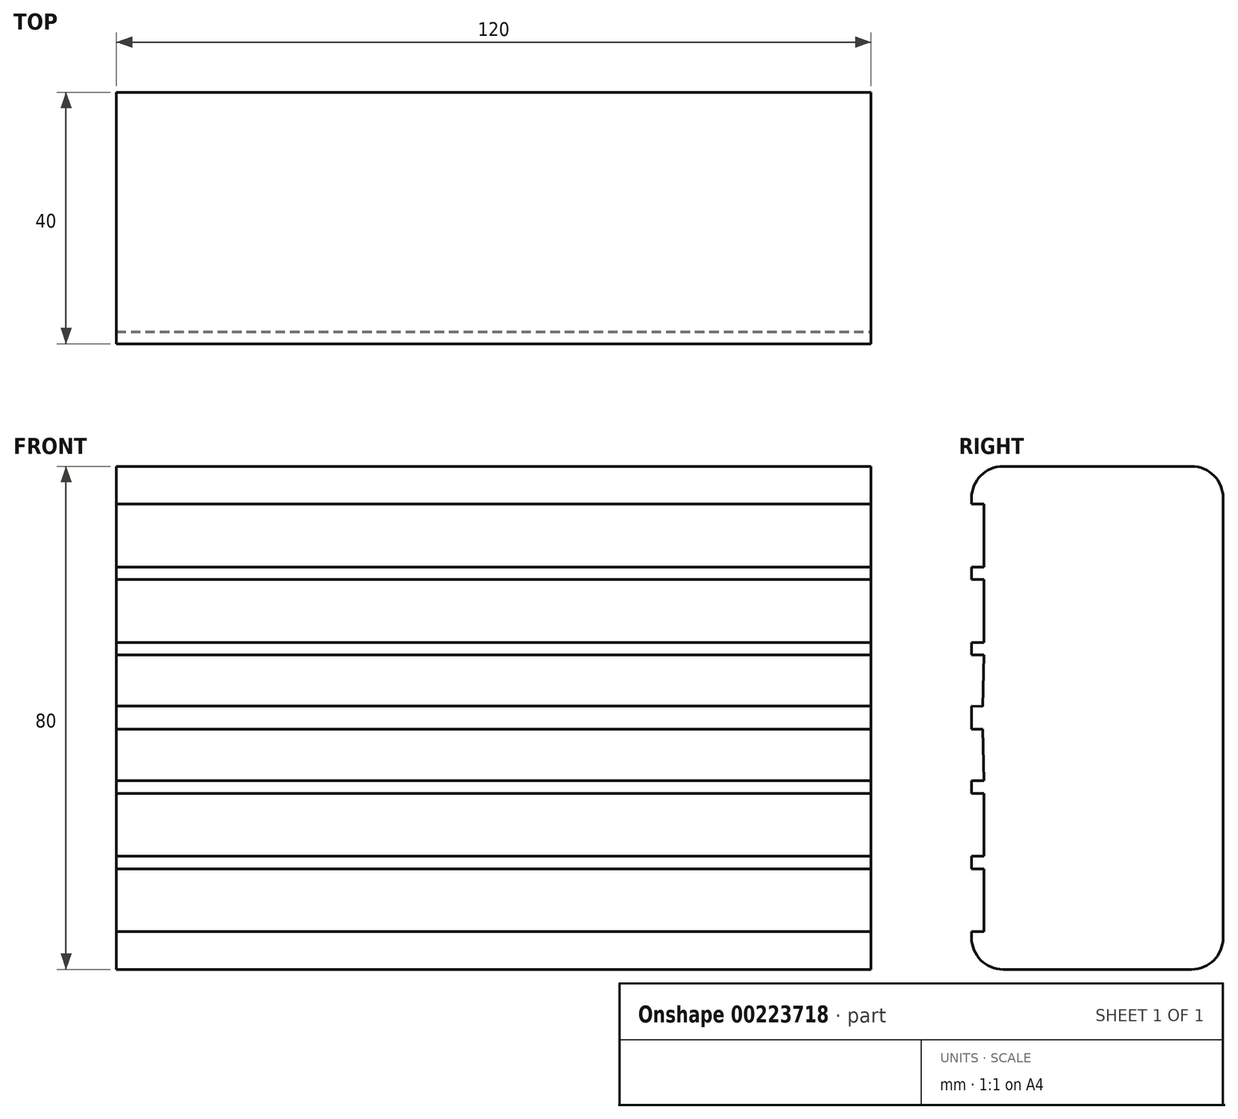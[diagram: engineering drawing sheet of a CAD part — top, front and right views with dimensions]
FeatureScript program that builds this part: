
annotation { "Feature Type Name" : "Feature", "Feature Type Description" : "" }
export const myFeature = defineFeature(function(context is Context, id is Id, definition is map)
    precondition{}
    {
        {
            var Q0;
            Q0=qCreatedBy(makeId("Front.planeOp"),FACE);
            var sketch = newSketch(context, id + "F0", { "sketchPlane" : qUnion([Q0])});
            skLineSegment(sketch, "E0.bottom", {"start": v(60, -40) * mm, "end": v(-60, -40) * mm});
            skLineSegment(sketch, "E0.top", {"start": v(60, 40) * mm, "end": v(-60, 40) * mm});
            skLineSegment(sketch, "E0.left", {"start": v(60, -40) * mm, "end": v(60, 40) * mm});
            skLineSegment(sketch, "E0.right", {"start": v(-60, -40) * mm, "end": v(-60, 40) * mm});
            skPoint(sketch, "E0.middle", {"position": v(0, 0) * mm});
            skSolve(sketch);
        }
        {
            var Q0;
            Q0=qSketchRegion(id+"F0",true);
            extrude(context, id + "F1", {"entities" : qUnion([Q0]), "depth" : 40 * mm});
        }
        {
            var Q0;
            Q0=makeQuery(id+"F1.opExtrude","CAP_EDGE",EDGE,{"disambiguationData":[OSD([sQuery(id+"F0.wireOp",EDGE,"E0.top")])],"isStart":false});
            var Q1;
            Q1=makeQuery(id+"F1.opExtrude","CAP_EDGE",EDGE,{"disambiguationData":[OSD([sQuery(id+"F0.wireOp",EDGE,"E0.bottom")])],"isStart":false});
            var Q2;
            Q2=makeQuery(id+"F1.opExtrude","CAP_EDGE",EDGE,{"disambiguationData":[OSD([sQuery(id+"F0.wireOp",EDGE,"E0.top")])],"isStart":true});
            var Q3;
            Q3=makeQuery(id+"F1.opExtrude","CAP_EDGE",EDGE,{"disambiguationData":[OSD([sQuery(id+"F0.wireOp",EDGE,"E0.bottom")])],"isStart":true});
            fillet(context, id + "F2", {"entities" : qUnion([Q0, Q1, Q2, Q3]), "radius" : 5 * mm, "tangentPropagation" : true, "allowEdgeOverflow" : false});
        }
        {
            var Q0;
            Q0=qCreatedBy(makeId("Right.planeOp"),FACE);
            var sketch = newSketch(context, id + "F3", { "sketchPlane" : qUnion([Q0])});
            skLineSegment(sketch, "E1", {"start": v(-38.2, 1.82) * mm, "end": v(-38.02, 10) * mm});
            skLineSegment(sketch, "E2", {"start": v(-38.02, 10) * mm, "end": v(-41.2, 10) * mm});
            skLineSegment(sketch, "E3", {"start": v(-41.2, 10) * mm, "end": v(-41.2, 12) * mm});
            skLineSegment(sketch, "E4", {"start": v(-41.2, 12) * mm, "end": v(-38.02, 12) * mm});
            skLineSegment(sketch, "E5", {"start": v(-38.02, 12) * mm, "end": v(-38.02, 22) * mm});
            skLineSegment(sketch, "E6", {"start": v(-38.02, 22) * mm, "end": v(-41.2, 22) * mm});
            skLineSegment(sketch, "E7", {"start": v(-41.2, 22) * mm, "end": v(-41.2, 24) * mm});
            skLineSegment(sketch, "E8", {"start": v(-41.2, 24) * mm, "end": v(-38.02, 24) * mm});
            skLineSegment(sketch, "E9", {"start": v(-38.02, 24) * mm, "end": v(-38.02, 34) * mm});
            skLineSegment(sketch, "E10", {"start": v(-38.02, 34) * mm, "end": v(-44.78, 34) * mm});
            skLineSegment(sketch, "E11", {"start": v(-44.78, 34) * mm, "end": v(-44.88, 1.82) * mm});
            skLineSegment(sketch, "E12.MirrorCS", {"start": v(-38.02, -10) * mm, "end": v(-41.2, -10) * mm});
            skLineSegment(sketch, "E13.MirrorCS", {"start": v(-41.2, -10) * mm, "end": v(-41.2, -12) * mm});
            skLineSegment(sketch, "E14.MirrorCS", {"start": v(-41.2, -12) * mm, "end": v(-38.02, -12) * mm});
            skLineSegment(sketch, "E15.MirrorCS", {"start": v(-41.2, -24) * mm, "end": v(-38.02, -24) * mm});
            skLineSegment(sketch, "E16.MirrorCS", {"start": v(-41.2, -22) * mm, "end": v(-41.2, -24) * mm});
            skLineSegment(sketch, "E17.MirrorCS", {"start": v(-38.02, -22) * mm, "end": v(-41.2, -22) * mm});
            skLineSegment(sketch, "E18.MirrorCS", {"start": v(-38.02, -12) * mm, "end": v(-38.02, -22) * mm});
            skLineSegment(sketch, "E19.MirrorCS", {"start": v(-38.02, -24) * mm, "end": v(-38.02, -34) * mm});
            skLineSegment(sketch, "E20.MirrorCS", {"start": v(-44.78, -34) * mm, "end": v(-44.88, -1.82) * mm});
            skLineSegment(sketch, "E21.MirrorCS", {"start": v(-38.02, -34) * mm, "end": v(-44.78, -34) * mm});
            skLineSegment(sketch, "E22.MirrorCS", {"start": v(-38.2, -1.82) * mm, "end": v(-38.02, -10) * mm});
            skLineSegment(sketch, "E23", {"start": v(-38.2, 1.82) * mm, "end": v(-41.37, 1.9) * mm});
            skLineSegment(sketch, "E24", {"start": v(-41.37, 1.9) * mm, "end": v(-41.37, -1.82) * mm});
            skLineSegment(sketch, "E25", {"start": v(-41.37, -1.82) * mm, "end": v(-38.2, -1.82) * mm});
            skLineSegment(sketch, "E26", {"start": v(-44.88, 1.82) * mm, "end": v(-44.88, -1.82) * mm});
            skSolve(sketch);
        }
        {
            var Q0;
            Q0=qSketchRegion(id+"F3",true);
            extrude(context, id + "F4", {"entities" : qUnion([Q0]), "operationType" : NewBodyOperationType.REMOVE, "endBound" : BoundingType.SYMMETRIC, "oppositeDirection" : true, "depth" : 200 * mm});
        }
    });
